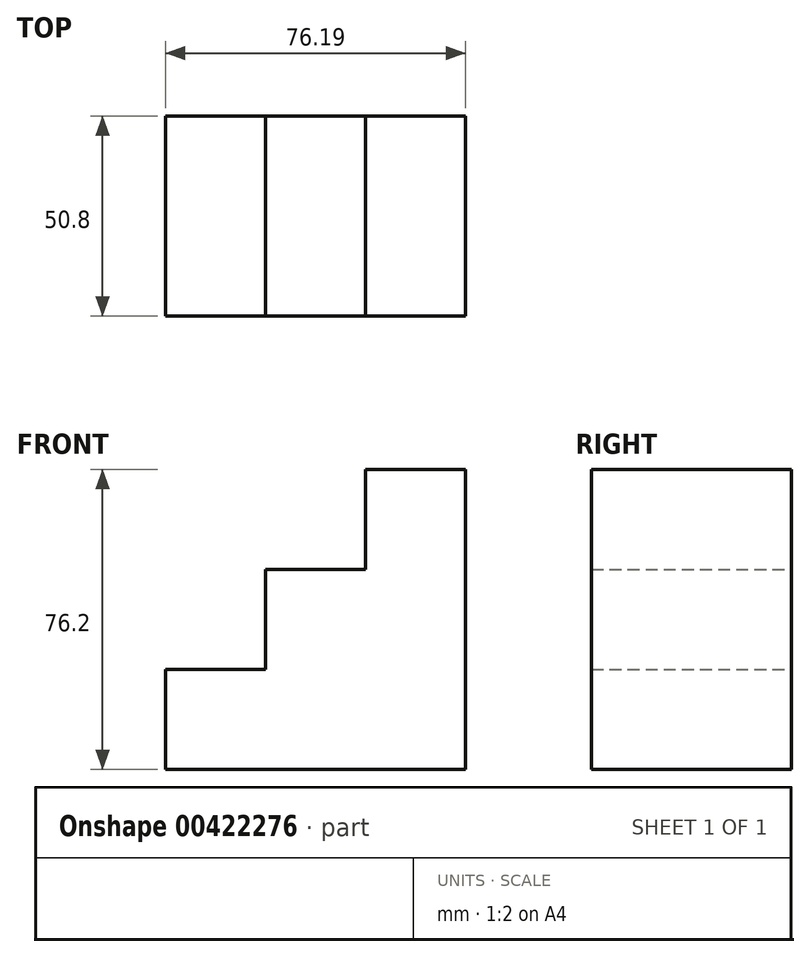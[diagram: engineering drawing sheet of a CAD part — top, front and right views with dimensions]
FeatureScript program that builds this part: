
annotation { "Feature Type Name" : "Feature", "Feature Type Description" : "" }
export const myFeature = defineFeature(function(context is Context, id is Id, definition is map)
    precondition{}
    {
        {
            var Q0;
            Q0=qCreatedBy(makeId("Front.planeOp"),FACE);
            var sketch = newSketch(context, id + "F0", { "sketchPlane" : qUnion([Q0])});
            skLineSegment(sketch, "E0", {"start": v(-43.54, -39.15) * mm, "end": v(32.65, -39.15) * mm});
            skLineSegment(sketch, "E1", {"start": v(32.65, -39.15) * mm, "end": v(32.65, 37.05) * mm});
            skLineSegment(sketch, "E2", {"start": v(32.65, 37.05) * mm, "end": v(7.26, 37.05) * mm});
            skLineSegment(sketch, "E3", {"start": v(7.26, 37.05) * mm, "end": v(7.26, 11.65) * mm});
            skLineSegment(sketch, "E4", {"start": v(7.26, 11.65) * mm, "end": v(-18.14, 11.65) * mm});
            skLineSegment(sketch, "E5", {"start": v(-18.14, 11.65) * mm, "end": v(-18.14, -13.75) * mm});
            skLineSegment(sketch, "E6", {"start": v(-18.14, -13.75) * mm, "end": v(-43.54, -13.75) * mm});
            skLineSegment(sketch, "E7", {"start": v(-43.54, -13.75) * mm, "end": v(-43.54, -39.15) * mm});
            skSolve(sketch);
        }
        {
            var Q0;
            Q0=makeQuery(id+"F0.imprint","IMPRINT",FACE,{"disambiguationData":[TD([[makeQuery(id+"F0.imprint","IMPRINT",EDGE,{"derivedFrom":sQuery(id+"F0.wireOp",EDGE,"E0")}),1.0]])]});
            extrude(context, id + "F1", {"entities" : qUnion([Q0]), "depth" : 50.8 * mm});
        }
    });
